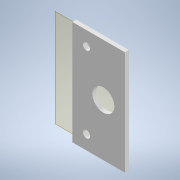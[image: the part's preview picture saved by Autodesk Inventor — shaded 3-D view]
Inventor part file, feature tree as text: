
AUTODESK INVENTOR PART (.ipt)
format: ipt  version: 2022 (Build 260153000, 153)  size: 199,168 bytes
history: native  units: mm
features: plane x6, sketch x5, extrude x5, reference x3, projected_geometry x3, other x3, mirror x1
ambient origin geometry x8: Origin, YZ Plane, XZ Plane, XY Plane, X Axis, Y Axis, Z Axis, Center Point
bodies: Solid1 (feature_tree)
feature tree (26):
  plane  "Work Plane1"
  sketch  "Sketch1"  dims[d0=0.2mm d3=5.0mm]
  plane  "Work Plane2"
  plane  "Work Plane3"
  extrude  "Extrusion1"  Depth=5.0mm
  sketch  "Sketch2"  dims[d4=5.0mm d5=5.0mm]
  plane  "Work Plane4"
  extrude  "Extrusion2"  Depth=5.0mm
  sketch  "Sketch3"  dims[d6=10.0mm d7=0.0mm d8=0.2mm]
  plane  "Work Plane5"
  plane  "Work Plane6"
  extrude  "Extrusion3"  Depth=10.0mm
  extrude  "Extrusion4"  Depth=10.0mm
  extrude  "Extrusion5"  Depth=10.0mm TaperAngle=0.0deg
  mirror  "Mirror1"
  reference  "Reference1"
  projected_geometry  "Projected Loop1"
  reference  "Reference2"
  reference  "Reference3"
  projected_geometry  "Projected Loop2"
  sketch  "Sketch4"  dims[d9=10.0mm d10=0.0mm d11=0.1mm]
  projected_geometry  "Projected Loop3"
  sketch  "Sketch5"  dims[d13=10.0mm d15=10.0mm d16=0.0mm d17=5.0mm d18=20.0mm d19=0.0mm d20=3.4mm d21=30.0mm d23=10.0mm d24=20.0mm d26=10.0mm d29=0.0mm d30=0.0mm]
  other  "Assembly2"
  other  "smol stepper:1"
  other  "paddle rotor:1"
